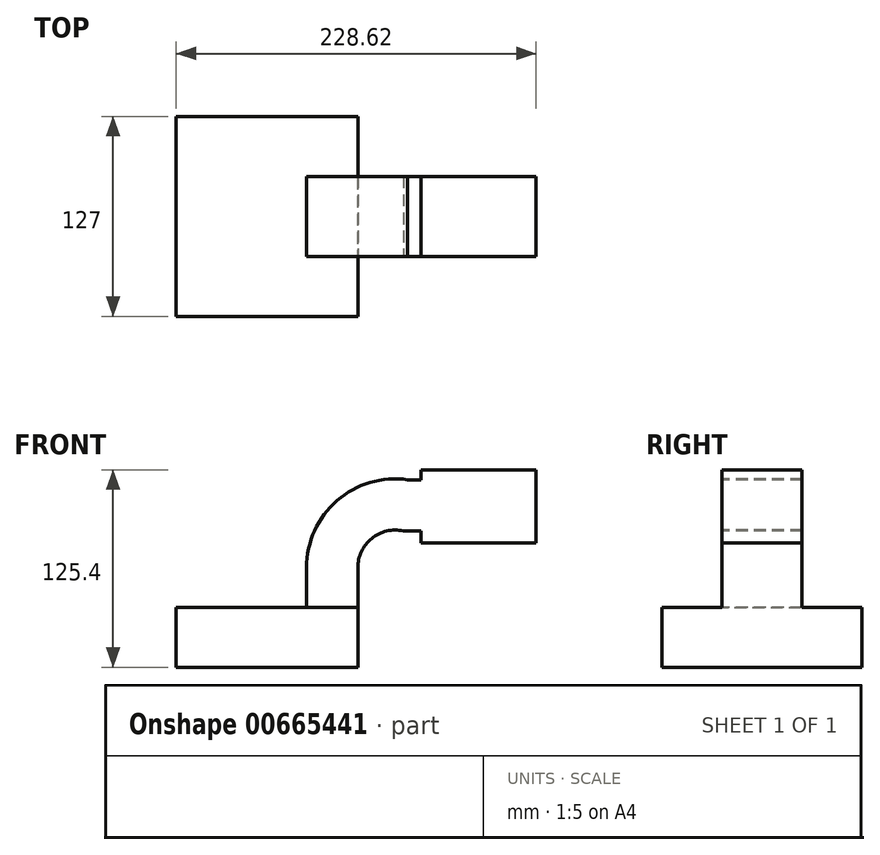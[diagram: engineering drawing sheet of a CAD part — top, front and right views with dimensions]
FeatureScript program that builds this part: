
annotation { "Feature Type Name" : "Feature", "Feature Type Description" : "" }
export const myFeature = defineFeature(function(context is Context, id is Id, definition is map)
    precondition{}
    {
        {
            var Q0;
            Q0=qCreatedBy(makeId("Front.planeOp"),FACE);
            var sketch = newSketch(context, id + "F0", { "sketchPlane" : qUnion([Q0])});
            skLineSegment(sketch, "E0.bottom", {"start": v(-57.68, -19.05) * mm, "end": v(57.68, -19.05) * mm});
            skLineSegment(sketch, "E0.top", {"start": v(-57.68, 19.05) * mm, "end": v(57.68, 19.05) * mm});
            skLineSegment(sketch, "E0.left", {"start": v(-57.68, -19.05) * mm, "end": v(-57.68, 19.05) * mm});
            skLineSegment(sketch, "E0.right", {"start": v(57.68, -19.05) * mm, "end": v(57.68, 19.05) * mm});
            skPoint(sketch, "E0.middle", {"position": v(0, 0) * mm});
            skLineSegment(sketch, "E1.bottom", {"start": v(170.94, 59.74) * mm, "end": v(97.7, 59.74) * mm});
            skLineSegment(sketch, "E1.top", {"start": v(170.94, 106.35) * mm, "end": v(97.7, 106.35) * mm});
            skLineSegment(sketch, "E1.left", {"start": v(170.94, 59.74) * mm, "end": v(170.94, 106.35) * mm});
            skLineSegment(sketch, "E1.right", {"start": v(97.7, 59.74) * mm, "end": v(97.7, 106.35) * mm});
            skPoint(sketch, "E1.middle", {"position": v(134.31, 83.05) * mm});
            skLineSegment(sketch, "E2", {"start": v(57.68, 19.05) * mm, "end": v(57.68, 44.2) * mm});
            skArc(sketch, "E3", {"start": v(57.68, 44.2) * mm, "mid": v(66.56, 62.77) * mm, "end": v(86.6, 67.5) * mm});
            skLineSegment(sketch, "E4", {"start": v(86.6, 67.5) * mm, "end": v(121, 67.5) * mm});
            skLineSegment(sketch, "E5.0", {"start": v(89.34, 100.02) * mm, "end": v(121, 100.02) * mm});
            skArc(sketch, "E5.1", {"start": v(25.17, 44.2) * mm, "mid": v(44.54, 86.73) * mm, "end": v(89.34, 100.02) * mm});
            skLineSegment(sketch, "E5.2", {"start": v(25.17, 19.05) * mm, "end": v(25.17, 44.2) * mm});
            skFitSpline(sketch, "E6", {"points": [v(-57.68, 19.05) * mm, v(97.7, 106.35) * mm, v(170.94, 59.74) * mm], "startDerivative": vector(289.02, 225.26) * mm, "endDerivative": vector(160.59, -167.16) * mm});
            skSolve(sketch);
        }
        {
            var Q0;
            Q0=makeQuery(id+"F0.imprint","IMPRINT",FACE,{"disambiguationData":[TD([[makeQuery(id+"F0.imprint","IMPRINT",EDGE,{"derivedFrom":sQuery(id+"F0.wireOp",EDGE,"E0.bottom")}),1.0]])]});
            extrude(context, id + "F1", {"entities" : qUnion([Q0]), "endBound" : BoundingType.SYMMETRIC, "depth" : 127 * mm, "offsetDistance" : 25.4 * mm});
        }
        {
            var Q0;
            {var subQ0=sQuery(id+"F0.wireOp",EDGE,"E1.top");Q0=makeQuery(id+"F0.imprint","IMPRINT",FACE,{"disambiguationData":[TD([[makeQuery(id+"F0.imprint","IMPRINT",EDGE,{"derivedFrom":subQ0}),1.0]])]});}
            var Q1;
            {var subQ3=sQuery(id+"F0.wireOp",EDGE,"E1.bottom");Q1=makeQuery(id+"F0.imprint","IMPRINT",FACE,{"disambiguationData":[TD([[makeQuery(id+"F0.imprint","IMPRINT",EDGE,{"derivedFrom":subQ3}),-1.0]])]});}
            var Q2;
            {var subQ0=sQuery(id+"F0.wireOp",EDGE,"E2");Q2=makeQuery(id+"F0.imprint","IMPRINT",FACE,{"disambiguationData":[TD([[makeQuery(id+"F0.imprint","IMPRINT",EDGE,{"derivedFrom":subQ0}),1.0]])]});}
            extrude(context, id + "F2", {"entities" : qUnion([Q0, Q1, Q2]), "operationType" : NewBodyOperationType.ADD, "endBound" : BoundingType.SYMMETRIC, "oppositeDirection" : true, "depth" : 50.8 * mm, "offsetDistance" : 25.4 * mm});
        }
        {
            var Q0;
            {var subQ0=sQuery(id+"F0.wireOp",EDGE,"E5.1");Q0=makeQuery(id+"F0.imprint","IMPRINT",FACE,{"disambiguationData":[TD([[makeQuery(id+"F0.imprint","IMPRINT",EDGE,{"derivedFrom":subQ0}),1.0]])]});}
            extrude(context, id + "F3", {"entities" : qUnion([Q0]), "operationType" : NewBodyOperationType.ADD, "depth" : 12.7 * mm, "offsetDistance" : 25.4 * mm});
        }
    });
